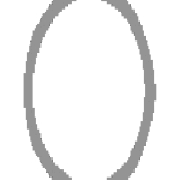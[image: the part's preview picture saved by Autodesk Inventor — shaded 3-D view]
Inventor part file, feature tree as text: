
AUTODESK INVENTOR PART (.ipt)
format: ipt  version: 2021 (Build 250183000, 183)  size: 112,128 bytes
history: native  units: in
note: dims shown in document units (in); Inventor stores cm internally (conversion verified against a paired STEP export)
features: other x4, sketch x3, plane x1
ambient origin geometry x8: Origin, YZ Plane, XZ Plane, XY Plane, X Axis, Y Axis, Z Axis, Center Point
bodies: Solid1 (feature_tree), Body (feature_tree)
feature tree (8):
  other  "Driven Length"
  other  "Frame Generator"
  other  "Start Plane"
  other  "End Plane"
  sketch  "Sketch"  dims[d2=16.9706in d4=-0.0in d5=16.9706in d6=0.12in d7=0.0in d8=90.0deg d9=16.9706in]
  sketch  "Sketch2"  dims[d0=1.0in]
  plane  "Work Plane3"
  sketch  "Sketch3"  dims[d1=0.065in]
